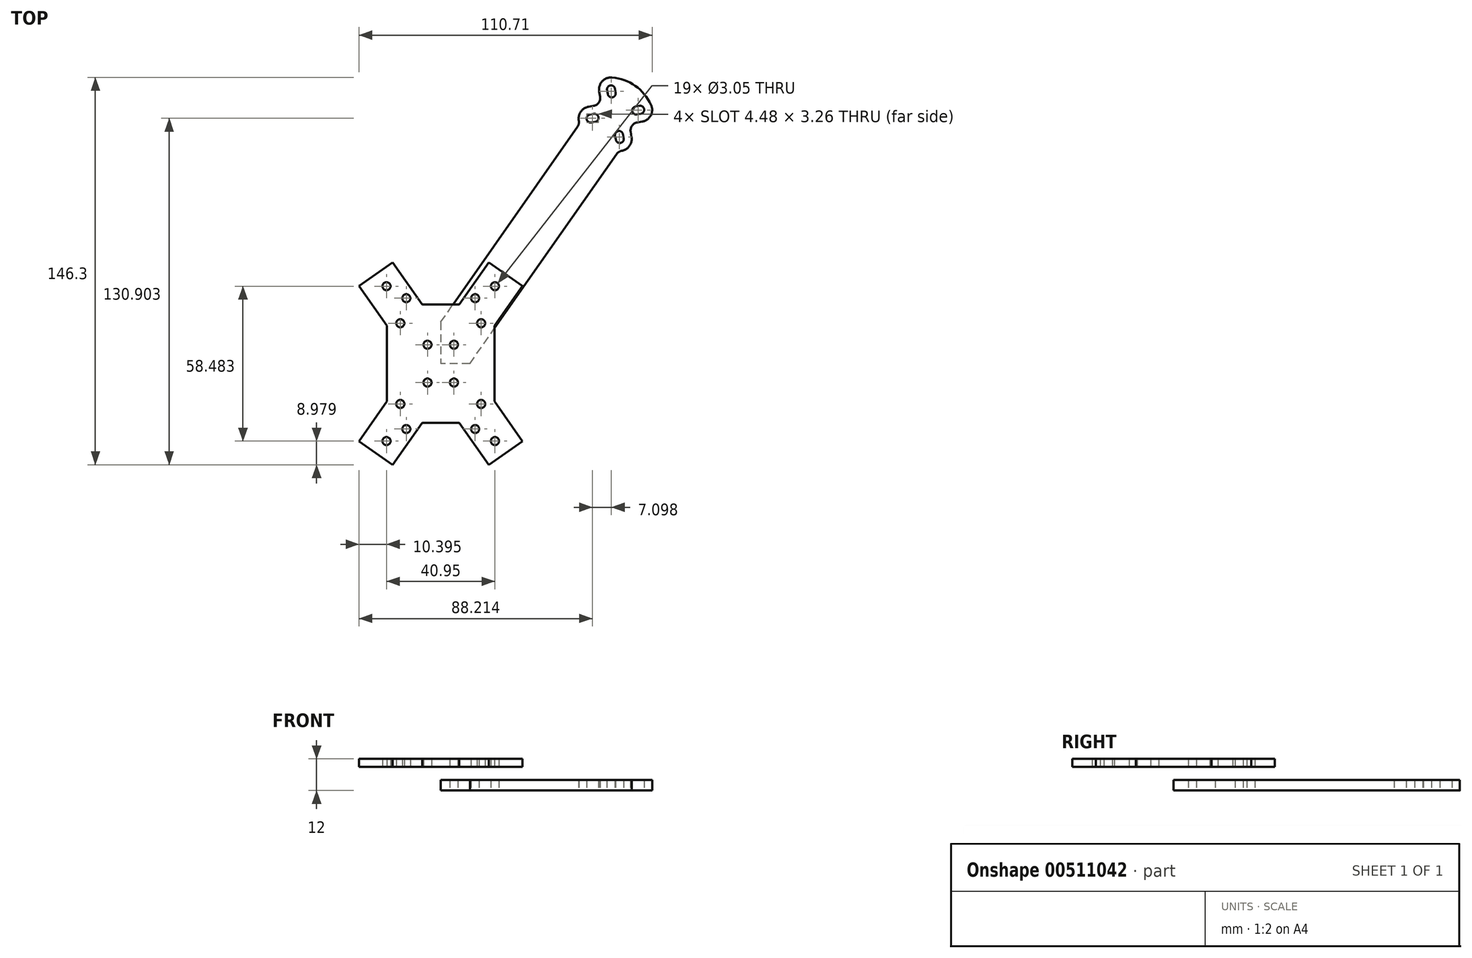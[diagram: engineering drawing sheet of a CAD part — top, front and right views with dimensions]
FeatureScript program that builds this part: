
annotation { "Feature Type Name" : "Feature", "Feature Type Description" : "" }
export const myFeature = defineFeature(function(context is Context, id is Id, definition is map)
    precondition{}
    {
        {
            var Q0;
            Q0=qCreatedBy(makeId("Top.planeOp"),FACE);
            var sketch = newSketch(context, id + "F0", { "sketchPlane" : qUnion([Q0])});
            skLineSegment(sketch, "E0", {"start": v(0, 0) * mm, "end": v(0, 103.1) * mm, "construction": true});
            skLineSegment(sketch, "E1", {"start": v(0, 0) * mm, "end": v(93.96, 0) * mm, "construction": true});
            skLineSegment(sketch, "E2", {"start": v(0, 0) * mm, "end": v(65.96, 94.2) * mm, "construction": true});
            skCircle(sketch, "E3", {"center": v(65.96, 94.2) * mm, "radius": 65 * mm, "construction": true});
            skCircle(sketch, "E4", {"center": v(20.48, 29.24) * mm, "radius": 1.52 * mm});
            skLineSegment(sketch, "E5", {"start": v(20, 0) * mm, "end": v(20, 7.5) * mm});
            skArc(sketch, "E6", {"start": v(25, 7.5) * mm, "mid": v(22.5, 10) * mm, "end": v(20, 7.5) * mm});
            skLineSegment(sketch, "E7", {"start": v(25, 7.5) * mm, "end": v(25, 0) * mm});
            skPoint(sketch, "E8.0.midPoint", {"position": v(83.17, 118.78) * mm});
            skCircle(sketch, "E9", {"center": v(5, 7.14) * mm, "radius": 1.52 * mm});
            skLineSegment(sketch, "E10", {"start": v(0, 15.7) * mm, "end": v(0, 0) * mm});
            skLineSegment(sketch, "E11", {"start": v(10.99, 0) * mm, "end": v(0, 0) * mm});
            skLineSegment(sketch, "E12", {"start": v(65.96, 94.2) * mm, "end": v(83.17, 118.78) * mm, "construction": true});
            skLineSegment(sketch, "E13", {"start": v(67.35, 86.32) * mm, "end": v(67.61, 84.85) * mm, "construction": true});
            skArc(sketch, "E14.0.startCap", {"start": v(65.85, 86.06) * mm, "mid": v(67.09, 87.83) * mm, "end": v(68.85, 86.59) * mm});
            skArc(sketch, "E14.0.endCap", {"start": v(69.11, 85.11) * mm, "mid": v(67.88, 83.34) * mm, "end": v(66.1, 84.58) * mm});
            skLineSegment(sketch, "E14.0.left", {"start": v(68.85, 86.59) * mm, "end": v(69.11, 85.11) * mm});
            skLineSegment(sketch, "E14.0.right", {"start": v(65.85, 86.06) * mm, "end": v(66.1, 84.58) * mm});
            skLineSegment(sketch, "E15", {"start": v(65.96, 94.2) * mm, "end": v(79.94, 84.41) * mm, "construction": true});
            skLineSegment(sketch, "E16.MirrorCS", {"start": v(73.57, 97.1) * mm, "end": v(75.05, 97.35) * mm});
            skArc(sketch, "E17.MirrorCS", {"start": v(73.57, 97.1) * mm, "mid": v(72.34, 95.33) * mm, "end": v(74.1, 94.09) * mm});
            skLineSegment(sketch, "E18.MirrorCS", {"start": v(73.84, 95.6) * mm, "end": v(75.32, 95.85) * mm, "construction": true});
            skLineSegment(sketch, "E19.MirrorCS", {"start": v(74.1, 94.09) * mm, "end": v(75.58, 94.35) * mm});
            skArc(sketch, "E20.MirrorCS", {"start": v(75.58, 94.35) * mm, "mid": v(76.82, 96.12) * mm, "end": v(75.05, 97.35) * mm});
            skLineSegment(sketch, "E21.MirrorCS", {"start": v(63.07, 101.82) * mm, "end": v(62.8, 103.3) * mm});
            skLineSegment(sketch, "E22.MirrorCS", {"start": v(66.07, 102.35) * mm, "end": v(65.81, 103.82) * mm});
            skLineSegment(sketch, "E23.MirrorCS", {"start": v(64.57, 102.08) * mm, "end": v(64.31, 103.56) * mm, "construction": true});
            skArc(sketch, "E24.MirrorCS", {"start": v(66.07, 102.35) * mm, "mid": v(64.84, 100.58) * mm, "end": v(63.07, 101.82) * mm});
            skArc(sketch, "E25.MirrorCS", {"start": v(62.8, 103.3) * mm, "mid": v(64.05, 105.06) * mm, "end": v(65.81, 103.82) * mm});
            skLineSegment(sketch, "E26.MirrorCS", {"start": v(57.82, 94.32) * mm, "end": v(56.34, 94.05) * mm});
            skArc(sketch, "E27.MirrorCS", {"start": v(56.34, 94.05) * mm, "mid": v(55.1, 92.29) * mm, "end": v(56.87, 91.05) * mm});
            skLineSegment(sketch, "E28.MirrorCS", {"start": v(58.08, 92.81) * mm, "end": v(56.6, 92.55) * mm, "construction": true});
            skArc(sketch, "E29.MirrorCS", {"start": v(58.35, 91.31) * mm, "mid": v(59.58, 93.08) * mm, "end": v(57.82, 94.32) * mm});
            skLineSegment(sketch, "E30.MirrorCS", {"start": v(58.35, 91.31) * mm, "end": v(56.87, 91.05) * mm});
            skCircle(sketch, "E31", {"center": v(13, 24.7) * mm, "radius": 1.52 * mm});
            skLineSegment(sketch, "E32", {"start": v(13, 24.7) * mm, "end": v(15.89, 22.69) * mm, "construction": true});
            skLineSegment(sketch, "E33", {"start": v(71.72, 87.58) * mm, "end": v(72.07, 85.63) * mm});
            skArc(sketch, "E34", {"start": v(68.36, 80.39) * mm, "mid": v(71.3, 82.24) * mm, "end": v(72.07, 85.63) * mm});
            skLineSegment(sketch, "E35", {"start": v(39.73, 72.44) * mm, "end": v(47.1, 67.27) * mm, "construction": true});
            skLineSegment(sketch, "E36", {"start": v(47.1, 67.27) * mm, "end": v(54.48, 62.11) * mm, "construction": true});
            skLineSegment(sketch, "E37", {"start": v(10.99, 0) * mm, "end": v(66.4, 79.15) * mm});
            skLineSegment(sketch, "E38", {"start": v(0, 15.7) * mm, "end": v(51.66, 89.47) * mm});
            skLineSegment(sketch, "E39.MirrorCS", {"start": v(74.16, 91.05) * mm, "end": v(76.1, 91.4) * mm});
            skArc(sketch, "E40.MirrorCS", {"start": v(79.43, 97.74) * mm, "mid": v(79.33, 93.75) * mm, "end": v(76.1, 91.4) * mm});
            skArc(sketch, "E41.MirrorCS", {"start": v(52.16, 91.73) * mm, "mid": v(52.89, 95.13) * mm, "end": v(55.82, 97) * mm});
            skLineSegment(sketch, "E42.MirrorCS", {"start": v(57.76, 97.35) * mm, "end": v(55.82, 97) * mm});
            skArc(sketch, "E43.MirrorCS", {"start": v(64.68, 108.07) * mm, "mid": v(60.97, 106.6) * mm, "end": v(59.86, 102.77) * mm});
            skLineSegment(sketch, "E44.MirrorCS", {"start": v(60.2, 100.83) * mm, "end": v(59.86, 102.77) * mm});
            skArc(sketch, "E45", {"start": v(79.43, 97.74) * mm, "mid": v(73.45, 104.9) * mm, "end": v(64.68, 108.07) * mm});
            skPoint(sketch, "E46.visualSharp", {"position": v(67.24, 80.34) * mm});
            skArc(sketch, "E46.filletArc", {"start": v(68.36, 80.39) * mm, "mid": v(67.26, 79.96) * mm, "end": v(66.4, 79.15) * mm});
            skPoint(sketch, "E47.visualSharp", {"position": v(52.5, 90.66) * mm});
            skArc(sketch, "E47.filletArc", {"start": v(51.66, 89.47) * mm, "mid": v(52.14, 90.55) * mm, "end": v(52.16, 91.73) * mm});
            skArc(sketch, "E48", {"start": v(57.76, 97.35) * mm, "mid": v(59.7, 98.59) * mm, "end": v(60.2, 100.83) * mm});
            skPoint(sketch, "E49.orphan", {"position": v(60.72, 97.87) * mm});
            skArc(sketch, "E50.MirrorCS", {"start": v(71.72, 87.58) * mm, "mid": v(72.22, 89.82) * mm, "end": v(74.16, 91.05) * mm});
            skPoint(sketch, "E51.orphan", {"position": v(71.2, 90.53) * mm});
            skSolve(sketch);
        }
        {
            var Q0;
            Q0=makeQuery(id+"F0.imprint","IMPRINT",FACE,{"disambiguationData":[TD([[makeQuery(id+"F0.imprint","IMPRINT",EDGE,{"derivedFrom":sQuery(id+"F0.wireOp",EDGE,"E4")}),-1.0]])]});
            var Q1;
            Q1=makeQuery(id+"F0.imprint","IMPRINT",FACE,{"disambiguationData":[TD([[makeQuery(id+"F0.imprint","IMPRINT",EDGE,{"derivedFrom":sQuery(id+"F0.wireOp",EDGE,"E8.0")}),1.0]])]});
            extrude(context, id + "F1", {"entities" : qUnion([Q0, Q1]), "depth" : 4 * mm, "offsetDistance" : 25 * mm});
        }
        {
            var Q0;
            Q0=makeQuery(id+"F1.opExtrude","CAP_FACE",FACE,{"disambiguationData":[OSD([sQuery(id+"F0.wireOp",EDGE,"E4"),sQuery(id+"F0.wireOp",EDGE,"w6Za7viU-XslT-eL26-v7qR-PVtx1nscPCrw"),sQuery(id+"F0.wireOp",EDGE,"m1q5n3BR-7mc0-eGyh-IMnw-hFcjK2Dm9aNC"),sQuery(id+"F0.wireOp",EDGE,"Wgtg9cnu-9r6v-fuNE-ovve-UqPkMIXU1x8r"),sQuery(id+"F0.wireOp",EDGE,"YulcCNTl-UrzR-zM0n-tjU8-OzW3QucuFuiJ"),sQuery(id+"F0.wireOp",EDGE,"8f8fb967-58a1-444d-b892-81b4f8ea902c1.MirrorCS"),sQuery(id+"F0.wireOp",EDGE,"8f8fb967-58a1-444d-b892-81b4f8ea902c2.MirrorCS"),sQuery(id+"F0.wireOp",EDGE,"68cdf088-86fb-4190-8a12-356bce8f52fc0.MirrorCS"),sQuery(id+"F0.wireOp",EDGE,"3fd3b338-187c-440d-b67b-80f1c3d15af10.MirrorCS"),sQuery(id+"F0.wireOp",EDGE,"ce2bb6fc-8b1a-4eb5-98e9-b79f73b76a321.MirrorCS"),sQuery(id+"F0.wireOp",EDGE,"ce2bb6fc-8b1a-4eb5-98e9-b79f73b76a322.MirrorCS"),sQuery(id+"F0.wireOp",EDGE,"ce2bb6fc-8b1a-4eb5-98e9-b79f73b76a324.MirrorCS"),sQuery(id+"F0.wireOp",EDGE,"ce2bb6fc-8b1a-4eb5-98e9-b79f73b76a325.MirrorCS"),sQuery(id+"F0.wireOp",EDGE,"ce2bb6fc-8b1a-4eb5-98e9-b79f73b76a326.MirrorCS"),sQuery(id+"F0.wireOp",EDGE,"ce2bb6fc-8b1a-4eb5-98e9-b79f73b76a327.MirrorCS"),sQuery(id+"F0.wireOp",EDGE,"ce2bb6fc-8b1a-4eb5-98e9-b79f73b76a328.MirrorCS"),sQuery(id+"F0.wireOp",EDGE,"ce2bb6fc-8b1a-4eb5-98e9-b79f73b76a329.MirrorCS"),sQuery(id+"F0.wireOp",EDGE,"E8.0"),sQuery(id+"F0.wireOp",EDGE,"E8.1"),sQuery(id+"F0.wireOp",EDGE,"E8.2"),sQuery(id+"F0.wireOp",EDGE,"E8.4"),sQuery(id+"F0.wireOp",EDGE,"E8.5"),sQuery(id+"F0.wireOp",EDGE,"ga3MCCmZ-KBx9-xbRN-8qVu-hq5lt1GVDJTu"),sQuery(id+"F0.wireOp",EDGE,"d7YvAnRK-XWlc-mF9K-xEkt-TTY3p4AQ4WQm"),sQuery(id+"F0.wireOp",EDGE,"66271485-31b6-4465-9533-eaafa0d02939.filletArc"),sQuery(id+"F0.wireOp",EDGE,"1444fb6f-7d19-4487-8c0e-7e828e170797.filletArc"),sQuery(id+"F0.wireOp",EDGE,"E9"),sQuery(id+"F0.wireOp",EDGE,"15iT6ud4-7Gir-Nnh9-CXTg-tOGej2BnBaeu"),sQuery(id+"F0.wireOp",EDGE,"E10"),sQuery(id+"F0.wireOp",EDGE,"E11")])],"isStart":false});
            cPlane(context, id + "F2", {"entities" : qUnion([Q0]), "cplaneType" : CPlaneType.OFFSET, "offset" : 5 * mm, "width" : 150 * mm, "height" : 150 * mm});
        }
        {
            var Q0;
            Q0=qCreatedBy(id+"F2.planeOp",FACE);
            var sketch = newSketch(context, id + "F3", { "sketchPlane" : qUnion([Q0])});
            skLineSegment(sketch, "E52.0", {"start": v(18.11, 38.22) * mm, "end": v(7, 22.35) * mm});
            skCircle(sketch, "E53.0", {"center": v(20.48, 29.24) * mm, "radius": 1.52 * mm});
            skCircle(sketch, "E54.0", {"center": v(5, 7.14) * mm, "radius": 1.52 * mm});
            skLineSegment(sketch, "E55.0", {"start": v(30.87, 29.29) * mm, "end": v(20.37, 14.28) * mm});
            skLineSegment(sketch, "E56", {"start": v(30.87, 29.29) * mm, "end": v(18.11, 38.22) * mm});
            skPoint(sketch, "E57.orphan", {"position": v(48.32, 81.35) * mm});
            skPoint(sketch, "E58.orphan", {"position": v(61.93, 73.65) * mm});
            skLineSegment(sketch, "E59", {"start": v(0, 0) * mm, "end": v(0, 38.1) * mm, "construction": true});
            skLineSegment(sketch, "E60", {"start": v(0, 0) * mm, "end": v(39.4, 0) * mm, "construction": true});
            skLineSegment(sketch, "E61", {"start": v(7, 22.35) * mm, "end": v(0, 22.35) * mm});
            skLineSegment(sketch, "E62", {"start": v(20.37, 14.28) * mm, "end": v(20.37, 0) * mm});
            skPoint(sketch, "E63.orphan", {"position": v(10.37, 0) * mm});
            skPoint(sketch, "E64.orphan", {"position": v(0, 12.35) * mm});
            skLineSegment(sketch, "E65.MirrorCS", {"start": v(30.87, -29.29) * mm, "end": v(18.11, -38.22) * mm});
            skLineSegment(sketch, "E66.MirrorCS", {"start": v(18.11, -38.22) * mm, "end": v(7, -22.35) * mm});
            skCircle(sketch, "E67.MirrorC", {"center": v(20.48, -29.24) * mm, "radius": 1.52 * mm});
            skCircle(sketch, "E68.MirrorC", {"center": v(5, -7.14) * mm, "radius": 1.52 * mm});
            skLineSegment(sketch, "E69.MirrorCS", {"start": v(7, -22.35) * mm, "end": v(0, -22.35) * mm});
            skLineSegment(sketch, "E70.MirrorCS", {"start": v(30.87, -29.29) * mm, "end": v(20.37, -14.28) * mm});
            skLineSegment(sketch, "E71.MirrorCS", {"start": v(20.37, -14.28) * mm, "end": v(20.37, 0) * mm});
            skLineSegment(sketch, "E72.MirrorCS", {"start": v(-30.87, -29.29) * mm, "end": v(-20.37, -14.28) * mm});
            skLineSegment(sketch, "E73.MirrorCS", {"start": v(-18.11, 38.22) * mm, "end": v(-7, 22.35) * mm});
            skLineSegment(sketch, "E74.MirrorCS", {"start": v(-7, -22.35) * mm, "end": v(0, -22.35) * mm});
            skCircle(sketch, "E75.MirrorC", {"center": v(-5, -7.14) * mm, "radius": 1.52 * mm});
            skCircle(sketch, "E76.MirrorC", {"center": v(-20.48, 29.24) * mm, "radius": 1.52 * mm});
            skCircle(sketch, "E77.MirrorC", {"center": v(-20.48, -29.24) * mm, "radius": 1.52 * mm});
            skLineSegment(sketch, "E78.MirrorCS", {"start": v(-30.87, 29.29) * mm, "end": v(-20.37, 14.28) * mm});
            skLineSegment(sketch, "E79.MirrorCS", {"start": v(-20.37, -14.28) * mm, "end": v(-20.37, 0) * mm});
            skPoint(sketch, "E80.MirrorP", {"position": v(-10.37, 0) * mm});
            skLineSegment(sketch, "E81.MirrorCS", {"start": v(-30.87, 29.29) * mm, "end": v(-18.11, 38.22) * mm});
            skCircle(sketch, "E82.MirrorC", {"center": v(-5, 7.14) * mm, "radius": 1.52 * mm});
            skLineSegment(sketch, "E83.MirrorCS", {"start": v(-18.11, -38.22) * mm, "end": v(-7, -22.35) * mm});
            skLineSegment(sketch, "E84.MirrorCS", {"start": v(-20.37, 14.28) * mm, "end": v(-20.37, 0) * mm});
            skLineSegment(sketch, "E85.MirrorCS", {"start": v(-30.87, -29.29) * mm, "end": v(-18.11, -38.22) * mm});
            skLineSegment(sketch, "E86.MirrorCS", {"start": v(-7, 22.35) * mm, "end": v(0, 22.35) * mm});
            skLineSegment(sketch, "E87", {"start": v(0, 0) * mm, "end": v(23.92, 34.16) * mm, "construction": true});
            skCircle(sketch, "E88", {"center": v(15.25, 15.25) * mm, "radius": 1.52 * mm});
            skCircle(sketch, "E89.MirrorC", {"center": v(15.25, -15.25) * mm, "radius": 1.52 * mm});
            skCircle(sketch, "E90.MirrorC", {"center": v(-15.25, 15.25) * mm, "radius": 1.52 * mm});
            skCircle(sketch, "E91.MirrorC", {"center": v(-15.25, -15.25) * mm, "radius": 1.52 * mm});
            skCircle(sketch, "E92.0", {"center": v(13, 24.7) * mm, "radius": 1.52 * mm});
            skCircle(sketch, "E93.MirrorC", {"center": v(13, -24.7) * mm, "radius": 1.52 * mm});
            skCircle(sketch, "E94.MirrorC", {"center": v(-13, 24.7) * mm, "radius": 1.52 * mm});
            skCircle(sketch, "E95.MirrorC", {"center": v(-13, -24.7) * mm, "radius": 1.52 * mm});
            skSolve(sketch);
        }
        {
            var Q0;
            Q0=makeQuery(id+"F3.imprint","IMPRINT",FACE,{"disambiguationData":[TD([[makeQuery(id+"F3.imprint","IMPRINT",EDGE,{"derivedFrom":sQuery(id+"F3.wireOp",EDGE,"E52.0")}),1.0]])]});
            extrude(context, id + "F4", {"entities" : qUnion([Q0]), "depth" : 3 * mm, "offsetDistance" : 25 * mm});
        }
    });
